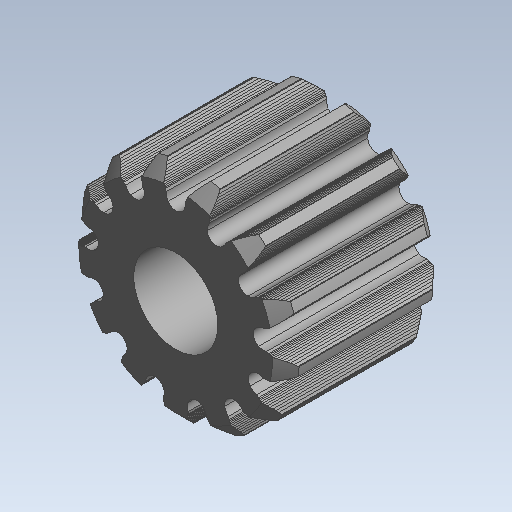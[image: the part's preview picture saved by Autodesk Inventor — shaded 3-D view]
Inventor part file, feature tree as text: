
AUTODESK INVENTOR PART (.ipt)
format: ipt  version: 2020 (Build 240168000, 168)  size: 698,880 bytes
history: native  units: mm (DEFAULTED — no unit token found)
features: mirror x1
ambient origin geometry x8: Origin, YZ Plane, XZ Plane, XY Plane, X Axis, Y Axis, Z Axis, Center Point
bodies: Solid1 (feature_tree)
feature tree (1):
  mirror  "Mirror5"
